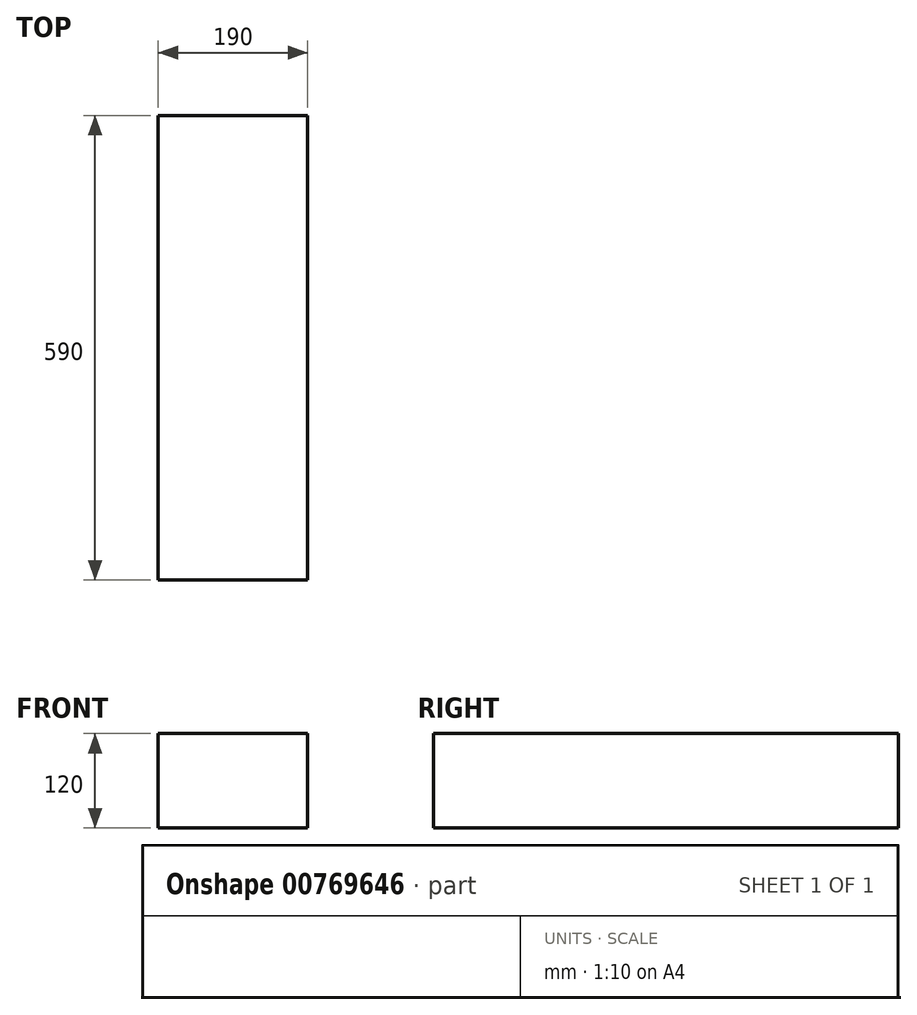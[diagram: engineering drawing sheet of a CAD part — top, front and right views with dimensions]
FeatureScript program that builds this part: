
annotation { "Feature Type Name" : "Feature", "Feature Type Description" : "" }
export const myFeature = defineFeature(function(context is Context, id is Id, definition is map)
    precondition{}
    {
        {
            var Q0;
            Q0=qCreatedBy(makeId("Front.planeOp"),FACE);
            var sketch = newSketch(context, id + "F0", { "sketchPlane" : qUnion([Q0])});
            skLineSegment(sketch, "E0.bottom", {"start": v(-73.68, 46.6) * mm, "end": v(116.32, 46.6) * mm});
            skLineSegment(sketch, "E0.top", {"start": v(-73.68, -73.4) * mm, "end": v(116.32, -73.4) * mm});
            skLineSegment(sketch, "E0.left", {"start": v(-73.68, 46.6) * mm, "end": v(-73.68, -73.4) * mm});
            skLineSegment(sketch, "E0.right", {"start": v(116.32, 46.6) * mm, "end": v(116.32, -73.4) * mm});
            skSolve(sketch);
        }
        {
            var Q0;
            Q0=makeQuery(id+"F0.imprint","IMPRINT",FACE,{"disambiguationData":[TD([[makeQuery(id+"F0.imprint","IMPRINT",EDGE,{"derivedFrom":sQuery(id+"F0.wireOp",EDGE,"E0.bottom")}),-1.0]])]});
            extrude(context, id + "F1", {"entities" : qUnion([Q0]), "depth" : 590 * mm, "offsetDistance" : 25 * mm});
        }
    });
